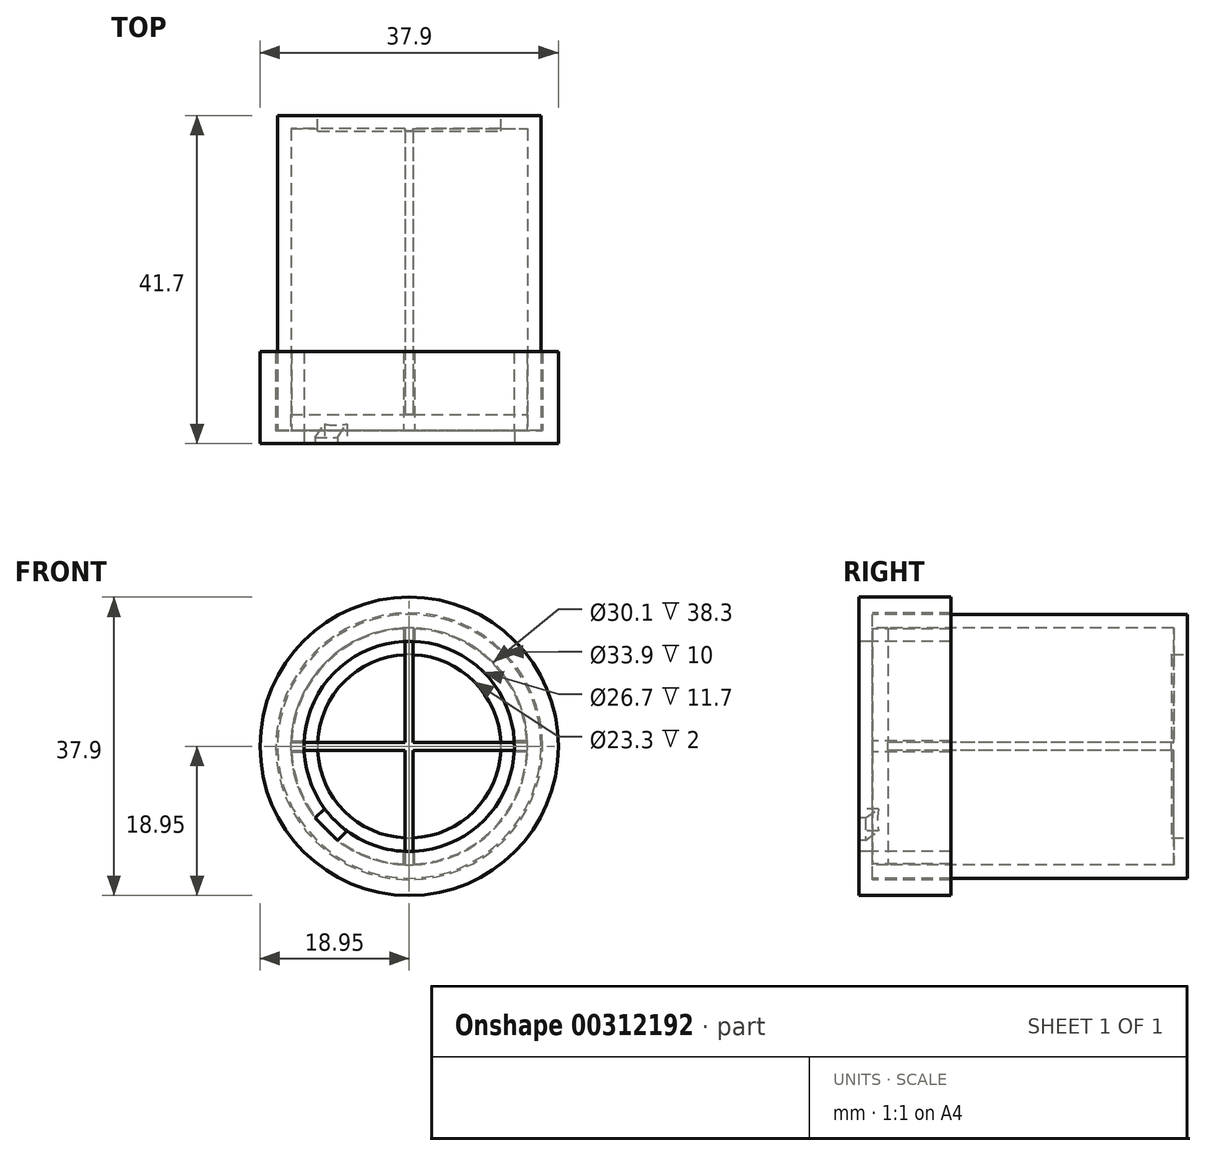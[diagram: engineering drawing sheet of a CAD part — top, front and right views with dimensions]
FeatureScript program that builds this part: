
annotation { "Feature Type Name" : "Feature", "Feature Type Description" : "" }
export const myFeature = defineFeature(function(context is Context, id is Id, definition is map)
    precondition{}
    {
        {
            var Q0;
            Q0=qCreatedBy(makeId("Front.planeOp"),FACE);
            var sketch = newSketch(context, id + "F0", { "sketchPlane" : qUnion([Q0])});
            skCircle(sketch, "E0", {"center": v(0, 0) * mm, "radius": 16.75 * mm});
            skSolve(sketch);
        }
        {
            var Q0;
            Q0 = qSketchRegion(id + "F0", true);
            extrude(context, id + "F1", {"entities" : qUnion([Q0]), "oppositeDirection" : true, "depth" : 40 * mm});
        }
        {
            var Q0;
            Q0=makeQuery(id+"F1.opExtrude","CAP_FACE",FACE,{"disambiguationData":[OSD([sQuery(id+"F0.wireOp",EDGE,"E0")])],"isStart":true});
            shell(context, id + "F2", {"entities" : qUnion([Q0]), "thickness" : 1.7 * mm});
        }
        {
            var Q0;
            Q0=makeQuery(id+"F1.opExtrude","CAP_FACE",FACE,{"disambiguationData":[OSD([sQuery(id+"F0.wireOp",EDGE,"E0")])],"isStart":true});
            cPlane(context, id + "F3", {"entities" : qUnion([Q0]), "cplaneType" : CPlaneType.OFFSET, "offset" : 2 * mm, "oppositeDirection" : true, "width" : 150 * mm, "height" : 150 * mm});
        }
        {
            var Q0;
            Q0=qCreatedBy(id+"F3.planeOp",FACE);
            var sketch = newSketch(context, id + "F4", { "sketchPlane" : qUnion([Q0])});
            skLineSegment(sketch, "E1", {"start": v(0, 15.6) * mm, "end": v(0, -15.6) * mm, "construction": true});
            skLineSegment(sketch, "E2", {"start": v(-15.8, 0) * mm, "end": v(15.97, 0) * mm, "construction": true});
            skLineSegment(sketch, "E3.0", {"start": v(-0.5, 15.6) * mm, "end": v(-0.5, -15.6) * mm});
            skLineSegment(sketch, "E4.0", {"start": v(0.5, 15.6) * mm, "end": v(0.5, -15.6) * mm});
            skLineSegment(sketch, "E5.0", {"start": v(-15.8, -0.5) * mm, "end": v(15.97, -0.5) * mm});
            skLineSegment(sketch, "E6.0", {"start": v(-15.8, 0.5) * mm, "end": v(15.97, 0.5) * mm});
            skLineSegment(sketch, "E7", {"start": v(-0.5, 15.6) * mm, "end": v(0.5, 15.6) * mm});
            skLineSegment(sketch, "E8", {"start": v(15.97, 0.5) * mm, "end": v(15.97, -0.5) * mm});
            skLineSegment(sketch, "E9", {"start": v(0.5, -15.6) * mm, "end": v(-0.5, -15.6) * mm});
            skLineSegment(sketch, "E10", {"start": v(-15.8, -0.5) * mm, "end": v(-15.8, 0.5) * mm});
            skSolve(sketch);
        }
        {
            var Q0;
            Q0 = qSketchRegion(id + "F4", true);
            var Q1;
            Q1=makeQuery(id+"F1.opExtrude","SWEPT_BODY",BODY,{"disambiguationData":[OSD([sQuery(id+"F0.wireOp",EDGE,"E0")])]});
            extrude(context, id + "F5", {"entities" : qUnion([Q0]), "operationType" : NewBodyOperationType.ADD, "endBound" : BoundingType.UP_TO_BODY, "oppositeDirection" : true, "endBoundEntityBody" : qUnion([Q1]), "depth" : 25 * mm});
        }
        {
            var Q0;
            Q0=makeQuery(id+"F1.opExtrude","CAP_FACE",FACE,{"disambiguationData":[OSD([sQuery(id+"F0.wireOp",EDGE,"E0")])],"isStart":true});
            var sketch = newSketch(context, id + "F6", { "sketchPlane" : qUnion([Q0])});
            skCircle(sketch, "E11", {"center": v(0, 0) * mm, "radius": 16.95 * mm});
            skCircle(sketch, "E12.0", {"center": v(0, 0) * mm, "radius": 18.95 * mm});
            skSolve(sketch);
        }
        {
            var Q0;
            Q0 = qSketchRegion(id + "F6", true);
            extrude(context, id + "F7", {"entities" : qUnion([Q0]), "oppositeDirection" : true, "depth" : 10 * mm});
        }
        {
            var Q0;
            Q0=makeQuery(id+"F1.opExtrude","CAP_FACE",FACE,{"disambiguationData":[OSD([sQuery(id+"F0.wireOp",EDGE,"E0")])],"isStart":true});
            var sketch = newSketch(context, id + "F8", { "sketchPlane" : qUnion([Q0])});
            skArc(sketch, "E13.0", {"start": v(-0.7, 15.03) * mm, "mid": v(-10.64, 10.64) * mm, "end": v(-15.03, 0.7) * mm, "construction": true});
            skLineSegment(sketch, "E14", {"start": v(-0.7, 14.93) * mm, "end": v(-0.7, 13.33) * mm});
            skLineSegment(sketch, "E15", {"start": v(-14.93, 0.7) * mm, "end": v(-13.33, 0.7) * mm});
            skArc(sketch, "E16.0", {"start": v(-0.7, 13.33) * mm, "mid": v(-9.44, 9.44) * mm, "end": v(-13.33, 0.7) * mm});
            skPoint(sketch, "E17.orphan", {"position": v(-15.04, 0.5) * mm});
            skPoint(sketch, "E18.orphan", {"position": v(-0.5, 15.04) * mm});
            skArc(sketch, "E19.0", {"start": v(-0.7, 14.93) * mm, "mid": v(-10.57, 10.57) * mm, "end": v(-14.93, 0.7) * mm});
            skSolve(sketch);
        }
        {
            var Q0;
            Q0 = qSketchRegion(id + "F8", true);
            extrude(context, id + "F9", {"entities" : qUnion([Q0]), "oppositeDirection" : true, "depth" : 7 * mm});
        }
        {
            var Q0;
            Q0 = qSketchRegion(id + "F8", true);
            extrude(context, id + "F10", {"entities" : qUnion([Q0]), "operationType" : NewBodyOperationType.ADD, "oppositeDirection" : true, "depth" : 10 * mm});
        }
        {
            var Q0;
            Q0=makeQuery(id+"F9.opExtrude","SWEPT_BODY",BODY,{"disambiguationData":[OSD([sQuery(id+"F8.wireOp",EDGE,"E14"),sQuery(id+"F8.wireOp",EDGE,"E15"),sQuery(id+"F8.wireOp",EDGE,"E16.0"),sQuery(id+"F8.wireOp",EDGE,"E19.0")])]});
            var Q1;
            Q1=makeQuery(id+"F1.opExtrude","CAP_EDGE",EDGE,{"disambiguationData":[OSD([sQuery(id+"F0.wireOp",EDGE,"E0")])],"isStart":true});
            circularPattern(context, id + "F11", {"entities" : qUnion([Q0]), "axis" : qUnion([Q1]), "angle" : 360 * degree, "instanceCount" : 4, "equalSpace" : true});
        }
        {
            var Q0;
            Q0=makeQuery(id+"F1.opExtrude","CAP_FACE",FACE,{"disambiguationData":[OSD([sQuery(id+"F0.wireOp",EDGE,"E0")])],"isStart":true});
            var sketch = newSketch(context, id + "F12", { "sketchPlane" : qUnion([Q0])});
            skCircle(sketch, "E20", {"center": v(0, 0) * mm, "radius": 13.35 * mm});
            skCircle(sketch, "E21.0", {"center": v(0, 0) * mm, "radius": 18.95 * mm});
            skSolve(sketch);
        }
        {
            var Q0;
            Q0 = qSketchRegion(id + "F12", true);
            extrude(context, id + "F13", {"entities" : qUnion([Q0]), "operationType" : NewBodyOperationType.ADD, "depth" : 1.7 * mm});
        }
        {
            var Q0;
            Q0=makeQuery(id+"F1.opExtrude","CAP_FACE",FACE,{"disambiguationData":[OSD([sQuery(id+"F0.wireOp",EDGE,"E0")])],"isStart":false});
            var sketch = newSketch(context, id + "F14", { "sketchPlane" : qUnion([Q0])});
            skCircle(sketch, "E22.0", {"center": v(0, 0) * mm, "radius": 11.65 * mm});
            skSolve(sketch);
        }
        {
            var Q0;
            Q0=makeQuery(id+"F14.imprint","IMPRINT",FACE,{"disambiguationData":[TD([[makeQuery(id+"F14.imprint","IMPRINT",EDGE,{"derivedFrom":sQuery(id+"F14.wireOp",EDGE,"E22.0")}),1.0]])]});
            extrude(context, id + "F15", {"entities" : qUnion([Q0]), "operationType" : NewBodyOperationType.REMOVE, "oppositeDirection" : true, "depth" : 2 * mm});
        }
        {
            var Q0;
            Q0=makeQuery(id+"F13.opExtrude","CAP_FACE",FACE,{"disambiguationData":[OSD([sQuery(id+"F12.wireOp",EDGE,"E20"),sQuery(id+"F12.wireOp",EDGE,"E21.0")])],"isStart":false});
            var sketch = newSketch(context, id + "F16", { "sketchPlane" : qUnion([Q0])});
            skLineSegment(sketch, "E23", {"start": v(-10.54, -10.54) * mm, "end": v(0, 0) * mm, "construction": true});
            skLineSegment(sketch, "E24", {"start": v(0, 0) * mm, "end": v(-21.6, 0) * mm, "construction": true});
            skLineSegment(sketch, "E25.0", {"start": v(-9.12, -11.95) * mm, "end": v(-5.59, -8.41) * mm});
            skLineSegment(sketch, "E26.0", {"start": v(-11.95, -9.12) * mm, "end": v(-8.41, -5.59) * mm});
            skLineSegment(sketch, "E27", {"start": v(-11.95, -9.12) * mm, "end": v(-9.12, -11.95) * mm});
            skLineSegment(sketch, "E28", {"start": v(-5.59, -8.41) * mm, "end": v(-8.41, -5.59) * mm});
            skSolve(sketch);
        }
        {
            var Q0;
            Q0 = qSketchRegion(id + "F16", true);
            extrude(context, id + "F17", {"entities" : qUnion([Q0]), "operationType" : NewBodyOperationType.REMOVE, "oppositeDirection" : true, "depth" : .8 * mm});
        }
        {
            var Q0;
            Q0=makeQuery(id+"F17.boolean.opBoolean","COPY",FACE,{"derivedFrom":makeQuery(id+"F17.opExtrude","SWEPT_FACE",FACE,{"disambiguationData":[OSD([sQuery(id+"F16.wireOp",EDGE,"E26.0")])]})});
            var sketch = newSketch(context, id + "F18", { "sketchPlane" : qUnion([Q0])});
            skLineSegment(sketch, "E29", {"start": v(-0.9, -14.9) * mm, "end": v(2.1, -11.9) * mm});
            skLineSegment(sketch, "E30", {"start": v(2.1, -11.9) * mm, "end": v(-0.9, -11.9) * mm});
            skLineSegment(sketch, "E31", {"start": v(-0.9, -11.9) * mm, "end": v(-0.9, -14.9) * mm});
            skSolve(sketch);
        }
        {
            var Q0;
            {var subQ0=sQuery(id+"F18.wireOp",EDGE,"E29");Q0=makeQuery(id+"F18.imprint","IMPRINT",FACE,{"disambiguationData":[TD([[makeQuery(id+"F18.imprint","IMPRINT",EDGE,{"derivedFrom":subQ0}),1.0]])]});}
            extrude(context, id + "F19", {"entities" : qUnion([Q0]), "operationType" : NewBodyOperationType.REMOVE, "depth" : 4 * mm});
        }
    });
